# Revit family: QF_COMENDA_6G3160_6G3267_CAT
name_source: partatom
category: Attrezzature speciali
units: mm (PartAtom-declared; Revit-internal decimal feet)

## family parameters
Basato su piano di lavoro = No
Condiviso = No
Numero OmniClass = 23.40.40.14
Punto di calcolo locali = No
Quota connettore circolare = Usa diametro
Sempre verticale = Sì
Taglio con vuoti quando caricato = No
Tipo di parte = Normale
Titolo OmniClass = Food Service Equipment

## types (2) — shared parameters
Altezza allacciamento elettrico da pavimento finito = 135 mm  [stored 0.442913 ft]
Altezza da terra raccordo acqua calda = 175 mm  [stored 0.574147 ft]
Altezza dello scarico diretto acqua da pavimento finito = 145 mm  [stored 0.475722 ft]
Corrente di funzionamento normale = 14 A
Descrizione = THREE-PHASE FRONT LOADING POTWASHER WITH RCD
Diametro dello scarico diretto di acqua = 1 1/2"
Diametro raccordo acqua calda = 1"
Fase = 3
Frequenza = 50 Hz
Lunghezza = 1020 mm  [stored 3.34646 ft]
Numero dei poli = 3
Peso netto = 230.00 kg
Potenza elettrica = 9000 W
Pressione minima acqua calda = 2000.0 Pa
Produttore = COMENDA
Profondità = 900 mm  [stored 2.95276 ft]
Protezione contro le sovracorrenti = 16 A
Temperatura raccomandata per acqua calda = 50 °C
Tensione = 400 V
URL = www.comenda.eu
URL catalogo = https://comenda.eu
zero-valued in all types: Prospetto di default

## per-type parameters (varying)
| type | Altezza | Modello |
| 6G3160 | 1870 mm | G-EVO 805 R RCD |
| 6G3267 | 2020 mm  [stored 6.6273 ft] | G-EVO 805H R RCD |

note: [stored X ft] marks values corroborated as IEEE doubles in the binary element streams (Revit-internal decimal feet)

## geometry (parser evidence)
native form markers: Sweep x4
no freeform markers — native parametric forms only
